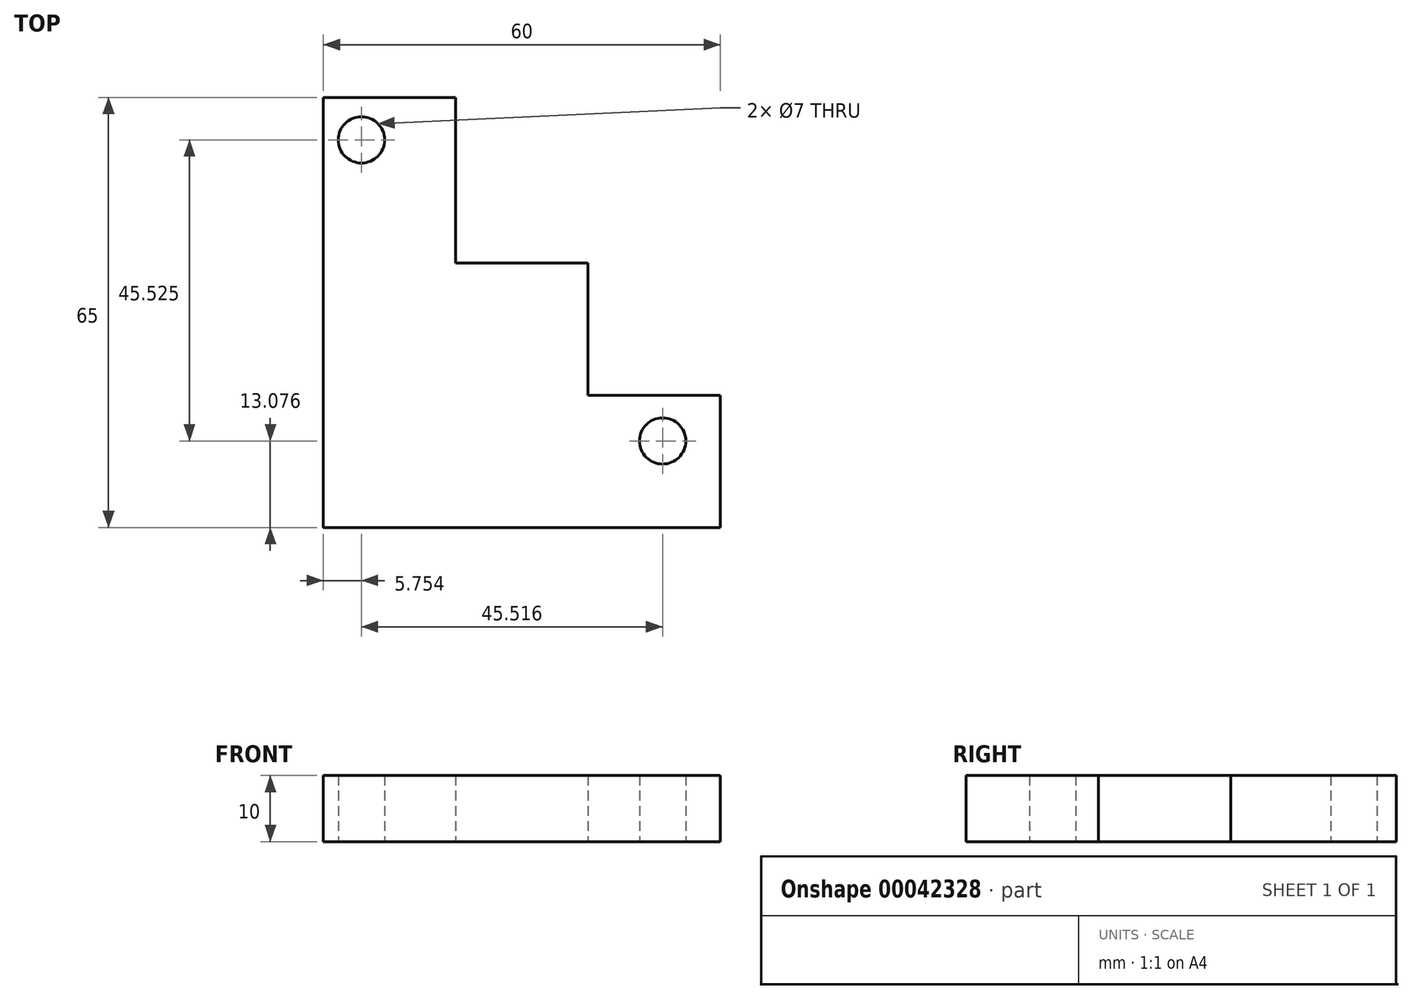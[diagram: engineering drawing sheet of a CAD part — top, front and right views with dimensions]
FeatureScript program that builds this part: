
annotation { "Feature Type Name" : "Feature", "Feature Type Description" : "" }
export const myFeature = defineFeature(function(context is Context, id is Id, definition is map)
    precondition{}
    {
        {
            var Q0;
            Q0=qCreatedBy(makeId("Top.planeOp"),FACE);
            var sketch = newSketch(context, id + "F0", { "sketchPlane" : qUnion([Q0])});
            skPoint(sketch, "E0.rect.middle", {"position": v(0, 0) * mm});
            skLineSegment(sketch, "E1.bottom", {"start": v(-45.2, 39.7) * mm, "end": v(-25.2, 39.7) * mm});
            skLineSegment(sketch, "E1.top", {"start": v(-45.2, 14.7) * mm, "end": v(-25.2, 14.7) * mm});
            skLineSegment(sketch, "E1.left", {"start": v(-45.2, 39.7) * mm, "end": v(-45.2, 14.7) * mm});
            skLineSegment(sketch, "E1.right", {"start": v(-25.2, 39.7) * mm, "end": v(-25.2, 14.7) * mm});
            skLineSegment(sketch, "E2.bottom", {"start": v(-45.2, 14.7) * mm, "end": v(-5.2, 14.7) * mm});
            skLineSegment(sketch, "E2.top", {"start": v(-45.2, -5.3) * mm, "end": v(-5.2, -5.3) * mm});
            skLineSegment(sketch, "E2.left", {"start": v(-45.2, 14.7) * mm, "end": v(-45.2, -5.3) * mm});
            skLineSegment(sketch, "E2.right", {"start": v(-5.2, 14.7) * mm, "end": v(-5.2, -5.3) * mm});
            skLineSegment(sketch, "E3.bottom", {"start": v(-45.2, -5.3) * mm, "end": v(14.8, -5.3) * mm});
            skLineSegment(sketch, "E3.top", {"start": v(-45.2, -25.3) * mm, "end": v(14.8, -25.3) * mm});
            skLineSegment(sketch, "E3.left", {"start": v(-45.2, -5.3) * mm, "end": v(-45.2, -25.3) * mm});
            skLineSegment(sketch, "E3.right", {"start": v(14.8, -5.3) * mm, "end": v(14.8, -25.3) * mm});
            skCircle(sketch, "E4", {"center": v(-39.45, 33.3) * mm, "radius": 3.5 * mm});
            skCircle(sketch, "E5", {"center": v(6.07, -12.22) * mm, "radius": 3.5 * mm});
            skSolve(sketch);
        }
        {
            var Q0;
            Q0=makeQuery(id+"F0.imprint","IMPRINT",FACE,{"disambiguationData":[TD([[makeQuery(id+"F0.imprint","IMPRINT",EDGE,{"derivedFrom":sQuery(id+"F0.wireOp",EDGE,"E1.bottom")}),-1.0]])]});
            var Q1;
            Q1=makeQuery(id+"F0.imprint","IMPRINT",FACE,{"disambiguationData":[TD([[makeQuery(id+"F0.imprint","IMPRINT",EDGE,{"derivedFrom":sQuery(id+"F0.wireOp",EDGE,"E3.top")}),1.0]])]});
            var Q2;
            {var subQ2=sQuery(id+"F0.wireOp",EDGE,"E2.left");Q2=makeQuery(id+"F0.imprint","IMPRINT",FACE,{"disambiguationData":[TD([[makeQuery(id+"F0.imprint","IMPRINT",EDGE,{"derivedFrom":subQ2}),1.0]])]});}
            extrude(context, id + "F1", {"entities" : qUnion([Q0, Q1, Q2]), "depth" : 10 * mm});
        }
    });
